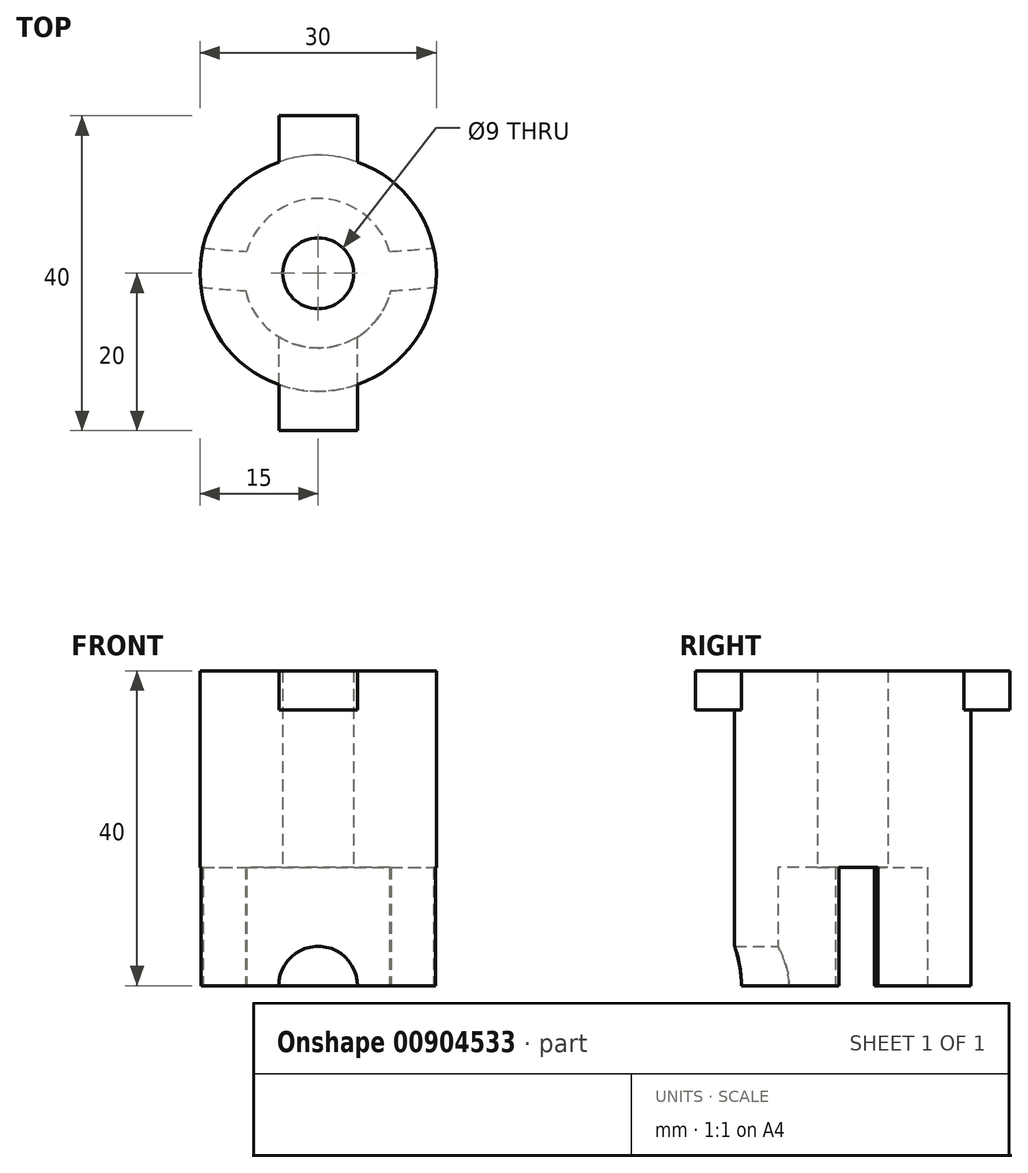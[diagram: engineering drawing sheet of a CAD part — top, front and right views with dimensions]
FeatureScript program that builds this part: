
annotation { "Feature Type Name" : "Feature", "Feature Type Description" : "" }
export const myFeature = defineFeature(function(context is Context, id is Id, definition is map)
    precondition{}
    {
        {
            var Q0;
            Q0=qCreatedBy(makeId("Top.planeOp"),FACE);
            var sketch = newSketch(context, id + "F0", { "sketchPlane" : qUnion([Q0])});
            skCircle(sketch, "E0", {"center": v(0, 0) * mm, "radius": 4.5 * mm});
            skCircle(sketch, "E1", {"center": v(0, 0) * mm, "radius": 15 * mm});
            skCircle(sketch, "E2", {"center": v(0, 0) * mm, "radius": 9.5 * mm});
            skLineSegment(sketch, "E3", {"start": v(5, 0) * mm, "end": v(-5, 0) * mm});
            skLineSegment(sketch, "E4", {"start": v(5, 0) * mm, "end": v(5, -8.08) * mm});
            skLineSegment(sketch, "E5", {"start": v(-5, 0) * mm, "end": v(-5, -8.08) * mm});
            skSolve(sketch);
        }
        {
            var Q0;
            Q0=qSketchRegion(id+"F0",true);
            var Q1;
            Q1=makeQuery(id+"F0.imprint","IMPRINT",FACE,{"disambiguationData":[TD([[makeQuery(id+"F0.imprint","IMPRINT",EDGE,{"derivedFrom":sQuery(id+"F0.wireOp",EDGE,"E0")}),-1.0]])]});
            extrude(context, id + "F1", {"entities" : qUnion([Q0, Q1]), "depth" : 40 * mm, "offsetDistance" : 25 * mm});
        }
        {
            var Q0;
            Q0=qCreatedBy(makeId("Front.planeOp"),FACE);
            var sketch = newSketch(context, id + "F2", { "sketchPlane" : qUnion([Q0])});
            skLineSegment(sketch, "E6.bottom", {"start": v(-5, 35) * mm, "end": v(5, 35) * mm});
            skLineSegment(sketch, "E6.top", {"start": v(-5, 40) * mm, "end": v(5, 40) * mm});
            skLineSegment(sketch, "E6.left", {"start": v(-5, 35) * mm, "end": v(-5, 40) * mm});
            skLineSegment(sketch, "E6.right", {"start": v(5, 35) * mm, "end": v(5, 40) * mm});
            skPoint(sketch, "E6.middle", {"position": v(0, 37.5) * mm});
            skSolve(sketch);
        }
        {
            var Q0;
            Q0=qSketchRegion(id+"F2",true);
            extrude(context, id + "F3", {"entities" : qUnion([Q0]), "operationType" : NewBodyOperationType.ADD, "depth" : 40 * mm, "offsetDistance" : 25 * mm, "symmetric" : true});
        }
        {
            var Q0;
            Q0=makeQuery(id+"F0.imprint","IMPRINT",FACE,{"disambiguationData":[TD([[makeQuery(id+"F0.imprint","IMPRINT",EDGE,{"derivedFrom":sQuery(id+"F0.wireOp",EDGE,"E0")}),-1.0]])]});
            extrude(context, id + "F4", {"entities" : qUnion([Q0]), "operationType" : NewBodyOperationType.REMOVE, "depth" : 15 * mm, "offsetDistance" : 25 * mm});
        }
        {
            var Q0;
            Q0=qCreatedBy(makeId("Front.planeOp"),FACE);
            var sketch = newSketch(context, id + "F5", { "sketchPlane" : qUnion([Q0])});
            skCircle(sketch, "E7", {"center": v(0, 0) * mm, "radius": 5 * mm});
            skSolve(sketch);
        }
        {
            var Q0;
            Q0=qSketchRegion(id+"F5",true);
            extrude(context, id + "F6", {"entities" : qUnion([Q0]), "operationType" : NewBodyOperationType.REMOVE, "depth" : 25 * mm, "offsetDistance" : 25 * mm});
        }
        {
            var Q0;
            Q0=qCreatedBy(makeId("Top.planeOp"),FACE);
            var sketch = newSketch(context, id + "F7", { "sketchPlane" : qUnion([Q0])});
            skCircle(sketch, "E8", {"center": v(0, 150) * mm, "radius": 152.5 * mm});
            skCircle(sketch, "E9", {"center": v(0, 150) * mm, "radius": 147.5 * mm});
            skSolve(sketch);
        }
        {
            var Q0;
            Q0=qSketchRegion(id+"F7",true);
            extrude(context, id + "F8", {"entities" : qUnion([Q0]), "operationType" : NewBodyOperationType.REMOVE, "depth" : 15 * mm, "offsetDistance" : 25 * mm});
        }
        {
            var Q0;
            Q0=makeQuery(id+"F3.boolean.opBoolean","SPLIT",FACE,{"disambiguationData":[TD([makeQuery(id+"F1.opExtrude","SWEPT_FACE",FACE,{"disambiguationData":[OSD([sQuery(id+"F0.wireOp",EDGE,"E0")])]})])],"derivedFrom":makeQuery(id+"F3.opExtrude","SWEPT_FACE",FACE,{"disambiguationData":[OSD([sQuery(id+"F2.wireOp",EDGE,"E6.bottom")])]})});
            extrude(context, id + "F9", {"entities" : qUnion([Q0]), "operationType" : NewBodyOperationType.REMOVE, "oppositeDirection" : true, "depth" : 25 * mm, "offsetDistance" : 25 * mm});
        }
    });
